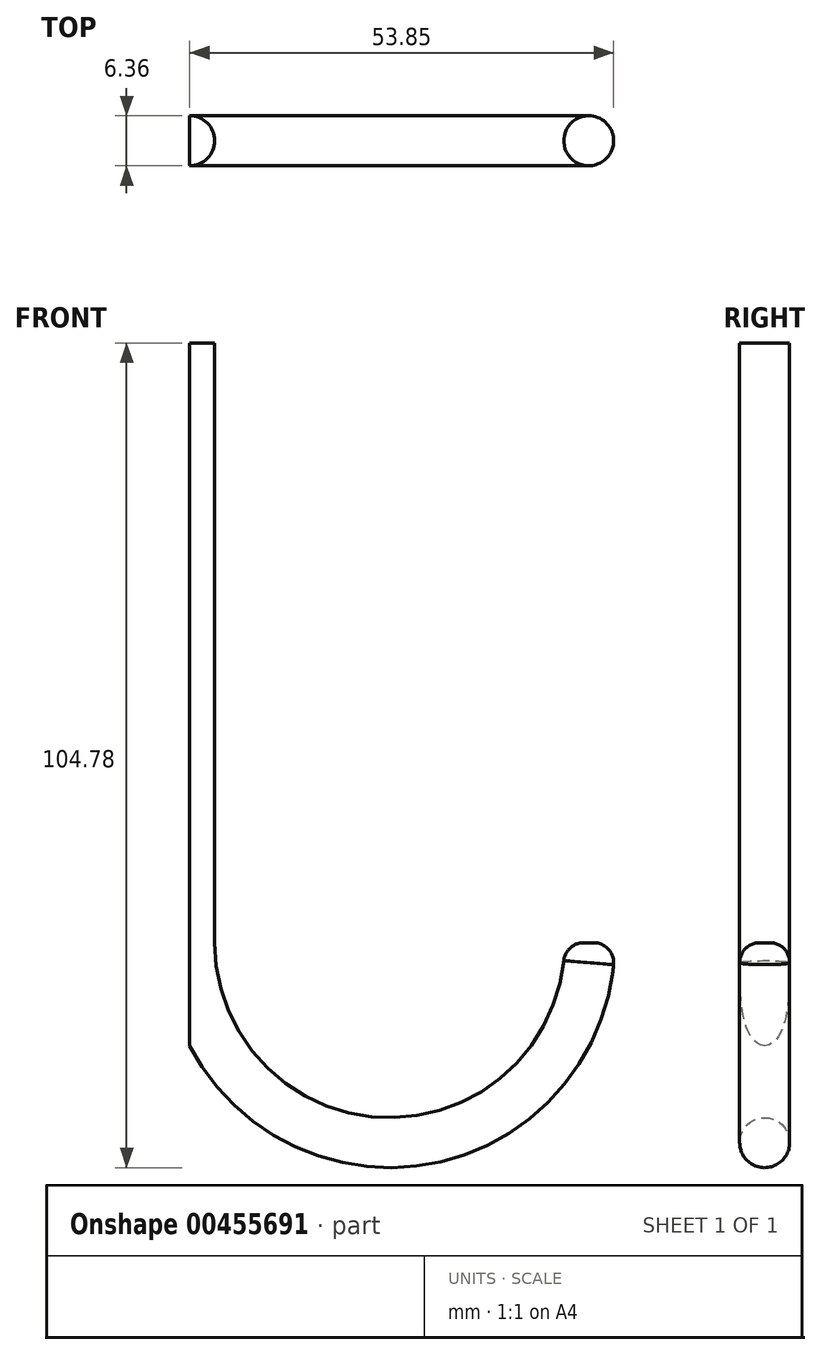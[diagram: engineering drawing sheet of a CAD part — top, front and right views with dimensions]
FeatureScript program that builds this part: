
annotation { "Feature Type Name" : "Feature", "Feature Type Description" : "" }
export const myFeature = defineFeature(function(context is Context, id is Id, definition is map)
    precondition{}
    {
        {
            var Q0;
            Q0=qCreatedBy(makeId("Front.planeOp"),FACE);
            var sketch = newSketch(context, id + "F0", { "sketchPlane" : qUnion([Q0])});
            skLineSegment(sketch, "E0", {"start": v(0, 0) * mm, "end": v(0, -76.2) * mm});
            skArc(sketch, "E1", {"start": v(0, -76.2) * mm, "mid": v(25.4, -101.6) * mm, "end": v(50.8, -76.2) * mm});
            skLineSegment(sketch, "E2", {"start": v(0, -76.2) * mm, "end": v(55.04, -76.2) * mm, "construction": true});
            skSolve(sketch);
        }
        {
            var Q0;
            Q0=qCreatedBy(makeId("Top.planeOp"),FACE);
            var Q1;
            Q1=sQuery(id+"F0.wireOp",VERTEX,"E1.end");
            cPlane(context, id + "F1", {"entities" : qUnion([Q0, Q1]), "cplaneType" : CPlaneType.PLANE_POINT, "offset" : 25.4 * mm, "width" : 152.4 * mm, "height" : 152.4 * mm});
        }
        {
            var Q0;
            Q0=qCreatedBy(id+"F1.planeOp",FACE);
            var sketch = newSketch(context, id + "F2", { "sketchPlane" : qUnion([Q0])});
            skPoint(sketch, "E3.0", {"position": v(50.8, 0) * mm});
            skPoint(sketch, "E3.1", {"position": v(0, 0) * mm});
            skCircle(sketch, "E4", {"center": v(50.8, 0) * mm, "radius": 3.18 * mm});
            skCircle(sketch, "E5", {"center": v(0, 0) * mm, "radius": 3.18 * mm});
            skSolve(sketch);
        }
        {
            var Q0;
            Q0=makeQuery(id+"F2.imprint","IMPRINT",FACE,{"disambiguationData":[TD([[makeQuery(id+"F2.imprint","IMPRINT",EDGE,{"derivedFrom":sQuery(id+"F2.wireOp",EDGE,"E4")}),1.0]])]});
            var Q1;
            Q1=sQuery(id+"F0.wireOp",EDGE,"E1");
            var Q2;
            Q2=sQuery(id+"F0.wireOp",EDGE,"E0");
            sweep(context, id + "F3", {"profiles" : qUnion([Q0]), "path" : qUnion([Q1, Q2])});
        }
        {
            var Q0;
            Q0=makeQuery(id+"F3.opSweep","CAP_EDGE",EDGE,{"disambiguationData":[OSD([sQuery(id+"F0.wireOp",VERTEX,"E1.end"),sQuery(id+"F2.wireOp",EDGE,"E4")])],"isStart":true});
            fillet(context, id + "F4", {"entities" : qUnion([Q0]), "radius" : 2.54 * mm, "tangentPropagation" : true, "allowEdgeOverflow" : false});
        }
        {
            var Q0;
            Q0=qCreatedBy(makeId("Right.planeOp"),FACE);
            var sketch = newSketch(context, id + "F5", { "sketchPlane" : qUnion([Q0])});
            skLineSegment(sketch, "E6.bottom", {"start": v(14.7, 15.74) * mm, "end": v(-19.91, 15.74) * mm});
            skLineSegment(sketch, "E6.top", {"start": v(14.7, -125.32) * mm, "end": v(-19.91, -125.32) * mm});
            skLineSegment(sketch, "E6.left", {"start": v(14.7, 15.74) * mm, "end": v(14.7, -125.32) * mm});
            skLineSegment(sketch, "E6.right", {"start": v(-19.91, 15.74) * mm, "end": v(-19.91, -125.32) * mm});
            skSolve(sketch);
        }
        {
            var Q0;
            Q0 = qSketchRegion(id + "F5", true);
            extrude(context, id + "F6", {"entities" : qUnion([Q0]), "operationType" : NewBodyOperationType.REMOVE, "oppositeDirection" : true, "depth" : 25.4 * mm});
        }
    });
